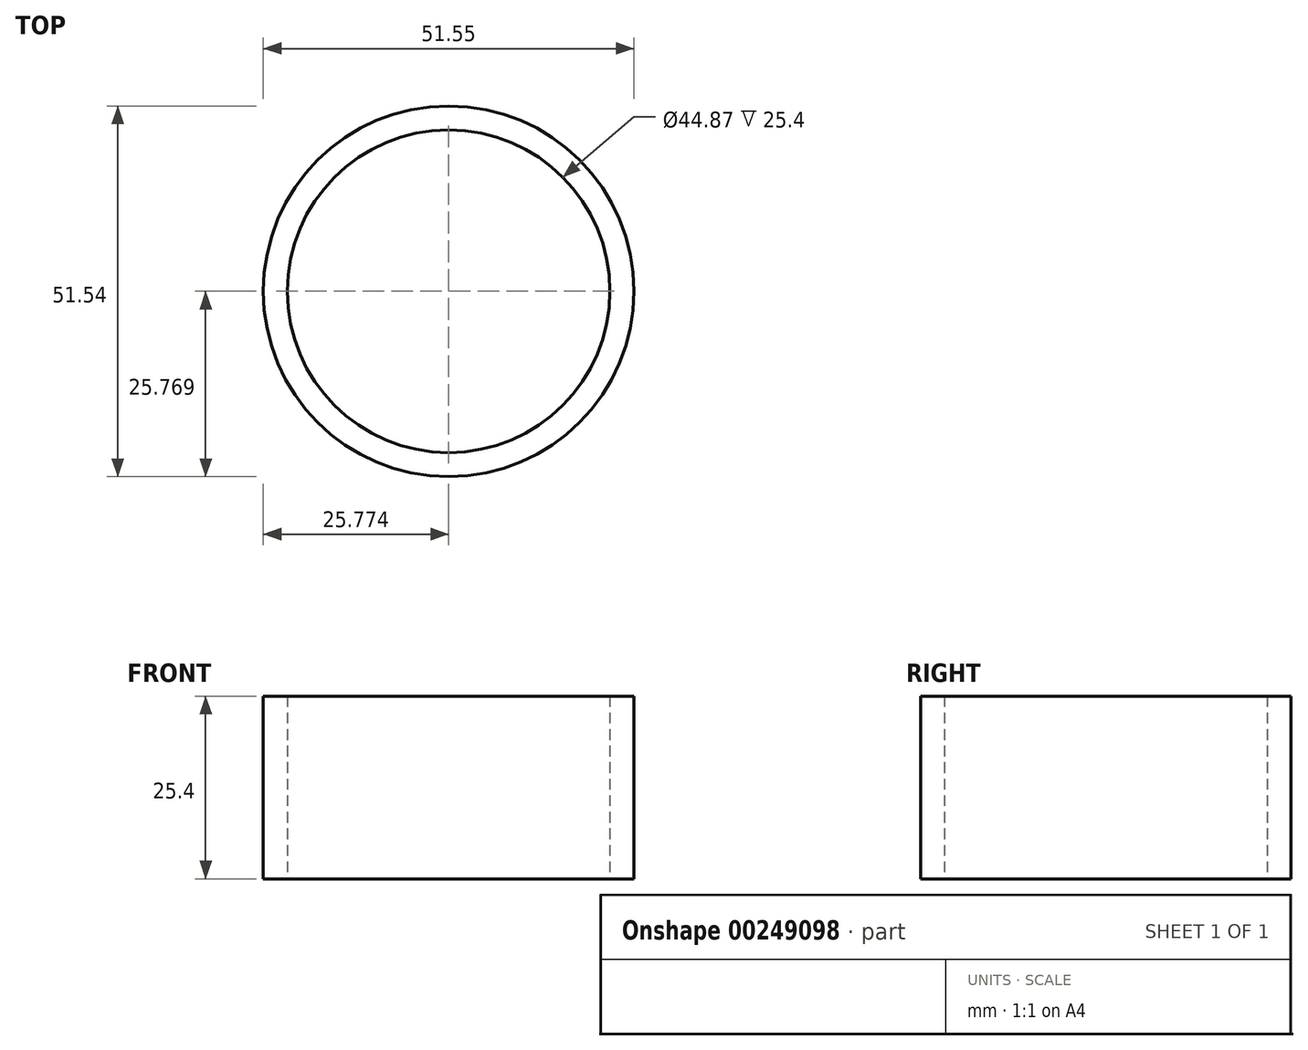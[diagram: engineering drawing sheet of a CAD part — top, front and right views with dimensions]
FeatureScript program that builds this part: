
annotation { "Feature Type Name" : "Feature", "Feature Type Description" : "" }
export const myFeature = defineFeature(function(context is Context, id is Id, definition is map)
    precondition{}
    {
        {
            var Q0;
            Q0=qCreatedBy(makeId("Top.planeOp"),FACE);
            var sketch = newSketch(context, id + "F0", { "sketchPlane" : qUnion([Q0])});
            skCircle(sketch, "E0", {"center": v(-13.83, 24.48) * mm, "radius": 25.77 * mm});
            skCircle(sketch, "E1", {"center": v(-13.83, 24.48) * mm, "radius": 22.43 * mm});
            skSolve(sketch);
        }
        {
            var Q0;
            Q0=makeQuery(id+"F0.imprint","IMPRINT",FACE,{"disambiguationData":[TD([[makeQuery(id+"F0.imprint","IMPRINT",EDGE,{"derivedFrom":sQuery(id+"F0.wireOp",EDGE,"E0")}),1.0]])]});
            extrude(context, id + "F1", {"entities" : qUnion([Q0]), "depth" : 25.4 * mm});
        }
    });
